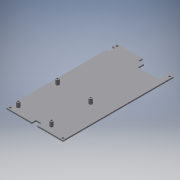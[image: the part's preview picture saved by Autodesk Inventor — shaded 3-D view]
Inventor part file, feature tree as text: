
AUTODESK INVENTOR PART (.ipt)
format: ipt  version: 2016 (Build 200138000, 138)  size: 208,384 bytes
history: native  units: in
note: dims shown in document units (in); Inventor stores cm internally (conversion verified against a paired STEP export)
features: extrude x5, sketch x4, chamfer x1
ambient origin geometry x8: Origin, YZ Plane, XZ Plane, XY Plane, X Axis, Y Axis, Z Axis, Center Point
bodies: Body1 (feature_tree)
feature tree (10):
  extrude  "Extrusion2"  Depth=0.0394in
  extrude  "Extrusion3"  TaperAngle=0.0deg  [1 undecoded]
  extrude  "Extrusion4"  Depth=0.0787in TaperAngle=0.0deg
  extrude  "Extrusion7"  Depth=0.1181in
  extrude  "Extrusion8"  Depth=0.1181in
  chamfer  "Chamfer1"  Distance=0.1181in
  sketch  "Sketch1"  dims[d0=0.0394in d4=0.0394in d5=0.0394in d6=0.0394in d7=0.0394in d10=0.0394in d12=0.0394in d13=0.0394in d14=0.0394in d15=0.0394in]
  sketch  "Sketch2"  dims[d16=0.2362in d17=0.0in]
  sketch  "Sketch3"  dims[d18=0.0in d21=0.0787in d22=0.0in]
  sketch  "Sketch6"  dims[d25=0.0394in d26=0.1181in d27=0.1181in d28=0.1181in d29=0.3937in d30=0.0in d31=1.9291in d32=2.2835in d33=1.9291in d34=2.2835in d35=0.3937in d36=0.3937in d37=0.315in d38=0.315in d39=0.2756in d40=0.0in d63=0.2756in d64=0.1575in d65=0.3543in d66=0.2756in d67=0.3543in d68=0.3937in d69=0.0in d70=0.2362in d71=0.2362in d72=0.2362in d73=0.2362in d75=6.4567in d76=6.4567in d77=6.5354in d79=1.2992in d82=1.2992in d83=0.1575in d92=0.3937in d93=0.0in d94=0.5906in d95=0.0in d96=3.3858in d97=0.0394in d98=3.3858in d99=0.0787in d100=0.0787in d101=45.0deg]
note: 1 required parameter value undecoded (feature->parameter linkage not recoverable at this tier; creation-order binding heuristic only, values carry confidence <= 0.55)
